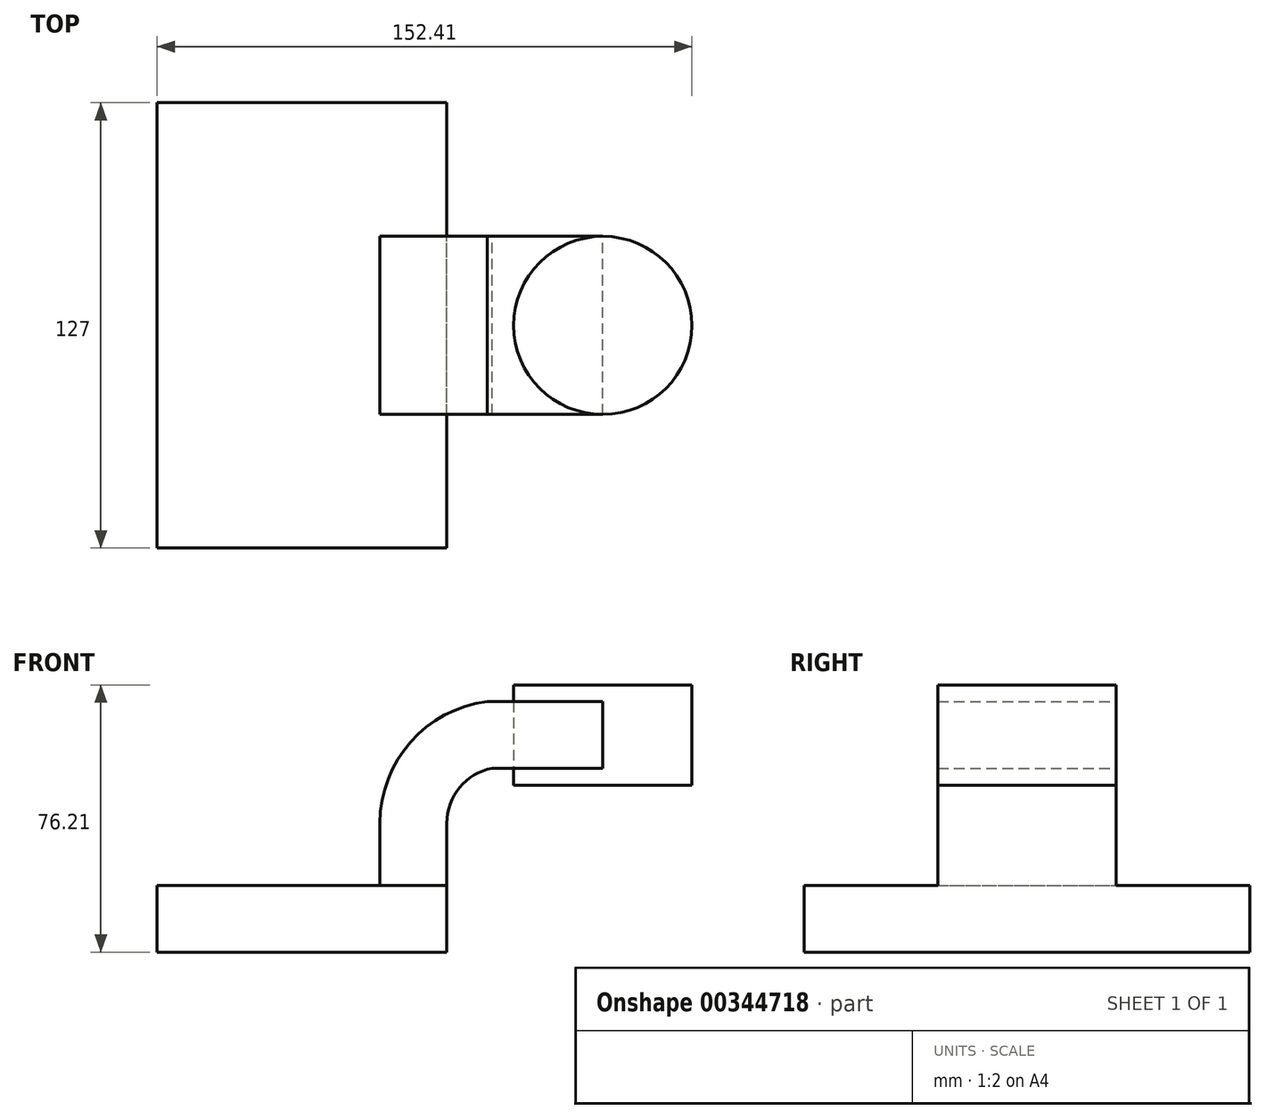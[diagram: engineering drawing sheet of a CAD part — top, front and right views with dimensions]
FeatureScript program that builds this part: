
annotation { "Feature Type Name" : "Feature", "Feature Type Description" : "" }
export const myFeature = defineFeature(function(context is Context, id is Id, definition is map)
    precondition{}
    {
        {
            var Q0;
            Q0=qCreatedBy(makeId("Front.planeOp"),FACE);
            var sketch = newSketch(context, id + "F0", { "sketchPlane" : qUnion([Q0])});
            skLineSegment(sketch, "E0.bottom", {"start": v(41.28, -9.52) * mm, "end": v(-41.28, -9.52) * mm});
            skLineSegment(sketch, "E0.top", {"start": v(41.28, 9.53) * mm, "end": v(-41.28, 9.53) * mm});
            skLineSegment(sketch, "E0.left", {"start": v(41.28, -9.52) * mm, "end": v(41.28, 9.53) * mm});
            skLineSegment(sketch, "E0.right", {"start": v(-41.28, -9.52) * mm, "end": v(-41.28, 9.53) * mm});
            skPoint(sketch, "E0.middle", {"position": v(0, 0) * mm});
            skLineSegment(sketch, "E1", {"start": v(41.28, 9.53) * mm, "end": v(41.28, 27.27) * mm});
            skLineSegment(sketch, "E2.bottom", {"start": v(111.12, 38.1) * mm, "end": v(60.32, 38.1) * mm});
            skLineSegment(sketch, "E2.top", {"start": v(111.12, 66.68) * mm, "end": v(60.32, 66.68) * mm});
            skLineSegment(sketch, "E2.left", {"start": v(111.12, 38.1) * mm, "end": v(111.12, 66.68) * mm});
            skLineSegment(sketch, "E2.right", {"start": v(60.32, 38.1) * mm, "end": v(60.32, 66.68) * mm});
            skPoint(sketch, "E2.middle", {"position": v(85.72, 52.39) * mm});
            skArc(sketch, "E3", {"start": v(41.27, 27.27) * mm, "mid": v(44.94, 37.41) * mm, "end": v(54.24, 42.88) * mm});
            skLineSegment(sketch, "E4", {"start": v(54.24, 42.88) * mm, "end": v(85.72, 42.88) * mm});
            skLineSegment(sketch, "E5.0", {"start": v(52.83, 61.93) * mm, "end": v(85.72, 61.93) * mm});
            skArc(sketch, "E5.1", {"start": v(22.23, 27.27) * mm, "mid": v(30.97, 50.39) * mm, "end": v(52.83, 61.93) * mm});
            skLineSegment(sketch, "E5.2", {"start": v(22.23, 9.53) * mm, "end": v(22.23, 27.27) * mm});
            skFitSpline(sketch, "E6", {"points": [v(-41.28, 9.53) * mm, v(60.32, 66.68) * mm], "startDerivative": vector(1.31, 69.1) * mm, "endDerivative": vector(227.24, 17.54) * mm});
            skLineSegment(sketch, "E7", {"start": v(85.72, 38.1) * mm, "end": v(85.72, 66.68) * mm});
            skSolve(sketch);
        }
        {
            var Q0;
            Q0=makeQuery(id+"F0.imprint","IMPRINT",FACE,{"disambiguationData":[TD([[makeQuery(id+"F0.imprint","IMPRINT",EDGE,{"derivedFrom":sQuery(id+"F0.wireOp",EDGE,"E0.bottom")}),-1.0]])]});
            extrude(context, id + "F1", {"entities" : qUnion([Q0]), "endBound" : BoundingType.SYMMETRIC, "depth" : 127 * mm});
        }
        {
            var Q0;
            {var subQ1=sQuery(id+"F0.wireOp",EDGE,"E1");Q0=makeQuery(id+"F0.imprint","IMPRINT",FACE,{"disambiguationData":[TD([[makeQuery(id+"F0.imprint","IMPRINT",EDGE,{"derivedFrom":subQ1}),1.0]])]});}
            var Q1;
            {var subQ0=sQuery(id+"F0.wireOp",EDGE,"E4");var subQ1=sQuery(id+"F0.wireOp",EDGE,"E2.right");var subQ2=makeQuery(id+"F0.imprint","INTERSECT",VERTEX,{"derivedFrom":[subQ1,subQ0]});Q1=makeQuery(id+"F0.imprint","IMPRINT",FACE,{"disambiguationData":[TD([[makeQuery(id+"F0.imprint","IMPRINT",EDGE,{"disambiguationData":[TD([[subQ2,-1.0]])],"derivedFrom":subQ1}),-1.0]])]});}
            extrude(context, id + "F2", {"entities" : qUnion([Q0, Q1]), "operationType" : NewBodyOperationType.ADD, "endBound" : BoundingType.SYMMETRIC, "depth" : 50.8 * mm});
        }
        {
            var Q0;
            {var subQ0=sQuery(id+"F0.wireOp",EDGE,"E5.1");Q0=makeQuery(id+"F0.imprint","IMPRINT",FACE,{"disambiguationData":[TD([[makeQuery(id+"F0.imprint","IMPRINT",EDGE,{"derivedFrom":subQ0}),1.0]])]});}
            extrude(context, id + "F3", {"entities" : qUnion([Q0]), "operationType" : NewBodyOperationType.ADD, "endBound" : BoundingType.SYMMETRIC, "depth" : 15.88 * mm});
        }
        {
            var Q0;
            {var subQ4=sQuery(id+"F0.wireOp",EDGE,"E2.left");Q0=makeQuery(id+"F0.imprint","IMPRINT",FACE,{"disambiguationData":[TD([[makeQuery(id+"F0.imprint","IMPRINT",EDGE,{"derivedFrom":subQ4}),1.0]])]});}
            var Q1;
            Q1=sQuery(id+"F0.wireOp",EDGE,"E7");
            revolve(context, id + "F4", {"entities" : qUnion([Q0]), "axis" : qUnion([Q1]), "revolveType" : RevolveType.FULL});
        }
    });
